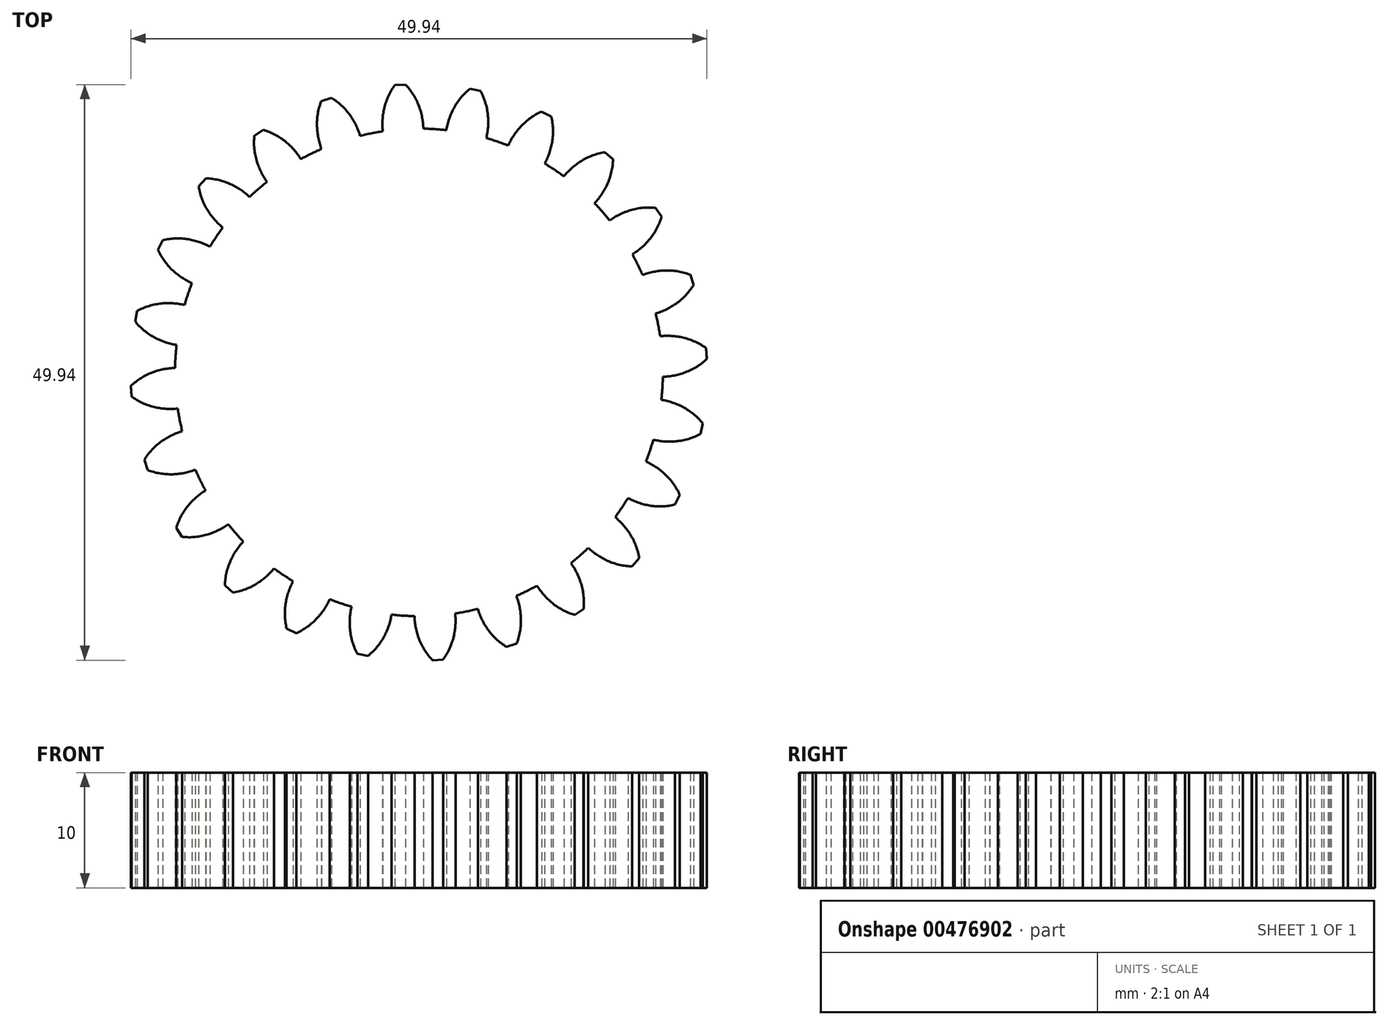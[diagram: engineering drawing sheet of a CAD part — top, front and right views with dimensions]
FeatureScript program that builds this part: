
annotation { "Feature Type Name" : "Feature", "Feature Type Description" : "" }
export const myFeature = defineFeature(function(context is Context, id is Id, definition is map)
    precondition{}
    {
        {
            var Q0;
            Q0=qCreatedBy(makeId("Top.planeOp"),FACE);
            var sketch = newSketch(context, id + "F0", { "sketchPlane" : qUnion([Q0])});
            skCircle(sketch, "E0", {"center": v(0, 0) * mm, "radius": 21.15 * mm});
            skCircle(sketch, "E1", {"center": v(0, 0) * mm, "radius": 23.1 * mm, "construction": true});
            skCircle(sketch, "E2", {"center": v(0, 0) * mm, "radius": 25 * mm, "construction": true});
            skLineSegment(sketch, "E3", {"start": v(0, 0) * mm, "end": v(0, 49.03) * mm, "construction": true});
            skLineSegment(sketch, "E4", {"start": v(0, 0) * mm, "end": v(-2.71, 41.35) * mm, "construction": true});
            skLineSegment(sketch, "E5", {"start": v(0, 23.1) * mm, "end": v(-29.6, 23.1) * mm, "construction": true});
            skLineSegment(sketch, "E6", {"start": v(-29.6, 23.1) * mm, "end": v(0, 23.1) * mm, "construction": true});
            skLineSegment(sketch, "E7", {"start": v(0, 23.1) * mm, "end": v(-33.56, 10.88) * mm, "construction": true});
            skCircle(sketch, "E8", {"center": v(0, 23.1) * mm, "radius": 5.75 * mm, "construction": true});
            skCircle(sketch, "E9", {"center": v(0, 0) * mm, "radius": 21.7 * mm, "construction": true});
            skArc(sketch, "E10", {"start": v(-1.67, 25.44) * mm, "mid": v(-9.32, 16.86) * mm, "end": v(-1.18, 24.97) * mm, "construction": true});
            skArc(sketch, "E11", {"start": v(0, 23.1) * mm, "mid": v(-0.5, 24.1) * mm, "end": v(-1.17, 24.97) * mm});
            skArc(sketch, "E12", {"start": v(0.38, 21.15) * mm, "mid": v(0.27, 22.14) * mm, "end": v(0, 23.1) * mm});
            skArc(sketch, "E13.MirrorCS", {"start": v(-3.14, 20.92) * mm, "mid": v(-3.16, 21.91) * mm, "end": v(-3.02, 22.9) * mm});
            skArc(sketch, "E14.MirrorCS", {"start": v(-3.02, 22.9) * mm, "mid": v(-2.66, 23.95) * mm, "end": v(-2.1, 24.91) * mm});
            skPoint(sketch, "E15.orphan", {"position": v(-1.67, 25.44) * mm});
            skLineSegment(sketch, "E16", {"start": v(-2.1, 24.91) * mm, "end": v(-1.17, 24.97) * mm});
            skArc(sketch, "E17.1.0", {"start": v(-8.84, 21.34) * mm, "mid": v(-8.77, 22.45) * mm, "end": v(-8.47, 23.52) * mm});
            skArc(sketch, "E17.1.1", {"start": v(-8.45, 19.4) * mm, "mid": v(-8.72, 20.35) * mm, "end": v(-8.84, 21.34) * mm});
            skArc(sketch, "E17.1.2", {"start": v(-5.98, 22.31) * mm, "mid": v(-6.71, 23.15) * mm, "end": v(-7.6, 23.82) * mm});
            skArc(sketch, "E17.1.3", {"start": v(-5.1, 20.53) * mm, "mid": v(-5.47, 21.46) * mm, "end": v(-5.98, 22.31) * mm});
            skLineSegment(sketch, "E17.1.4", {"start": v(-8.47, 23.52) * mm, "end": v(-7.6, 23.82) * mm});
            skArc(sketch, "E17.2.0", {"start": v(-14.06, 18.33) * mm, "mid": v(-14.28, 19.42) * mm, "end": v(-14.27, 20.52) * mm});
            skArc(sketch, "E17.2.1", {"start": v(-13.18, 16.54) * mm, "mid": v(-13.7, 17.4) * mm, "end": v(-14.06, 18.33) * mm});
            skArc(sketch, "E17.2.2", {"start": v(-11.55, 20) * mm, "mid": v(-12.47, 20.62) * mm, "end": v(-13.5, 21.04) * mm});
            skArc(sketch, "E17.2.3", {"start": v(-10.24, 18.5) * mm, "mid": v(-10.83, 19.3) * mm, "end": v(-11.55, 20) * mm});
            skLineSegment(sketch, "E17.2.4", {"start": v(-14.27, 20.52) * mm, "end": v(-13.5, 21.04) * mm});
            skArc(sketch, "E17.3.0", {"start": v(-18.33, 14.06) * mm, "mid": v(-18.82, 15.06) * mm, "end": v(-19.1, 16.13) * mm});
            skArc(sketch, "E17.3.1", {"start": v(-17, 12.57) * mm, "mid": v(-17.73, 13.26) * mm, "end": v(-18.33, 14.06) * mm});
            skArc(sketch, "E17.3.2", {"start": v(-16.33, 16.33) * mm, "mid": v(-17.39, 16.7) * mm, "end": v(-18.49, 16.83) * mm});
            skArc(sketch, "E17.3.3", {"start": v(-14.68, 15.22) * mm, "mid": v(-15.46, 15.85) * mm, "end": v(-16.33, 16.33) * mm});
            skLineSegment(sketch, "E17.3.4", {"start": v(-19.1, 16.13) * mm, "end": v(-18.49, 16.83) * mm});
            skArc(sketch, "E17.4.0", {"start": v(-21.34, 8.84) * mm, "mid": v(-22.07, 9.68) * mm, "end": v(-22.62, 10.64) * mm});
            skArc(sketch, "E17.4.1", {"start": v(-19.68, 7.74) * mm, "mid": v(-20.56, 8.22) * mm, "end": v(-21.34, 8.84) * mm});
            skArc(sketch, "E17.4.2", {"start": v(-20, 11.55) * mm, "mid": v(-21.11, 11.62) * mm, "end": v(-22.21, 11.47) * mm});
            skArc(sketch, "E17.4.3", {"start": v(-18.12, 10.9) * mm, "mid": v(-19.04, 11.3) * mm, "end": v(-20, 11.55) * mm});
            skLineSegment(sketch, "E17.4.4", {"start": v(-22.62, 10.64) * mm, "end": v(-22.21, 11.47) * mm});
            skArc(sketch, "E17.5.0", {"start": v(-22.9, 3.02) * mm, "mid": v(-23.82, 3.63) * mm, "end": v(-24.6, 4.42) * mm});
            skArc(sketch, "E17.5.1", {"start": v(-21.02, 2.38) * mm, "mid": v(-21.99, 2.62) * mm, "end": v(-22.9, 3.02) * mm});
            skArc(sketch, "E17.5.2", {"start": v(-22.31, 5.98) * mm, "mid": v(-23.4, 5.76) * mm, "end": v(-24.42, 5.33) * mm});
            skArc(sketch, "E17.5.3", {"start": v(-20.33, 5.84) * mm, "mid": v(-21.31, 6) * mm, "end": v(-22.31, 5.98) * mm});
            skLineSegment(sketch, "E17.5.4", {"start": v(-24.6, 4.42) * mm, "end": v(-24.42, 5.33) * mm});
            skArc(sketch, "E17.6.0", {"start": v(-22.9, -3.02) * mm, "mid": v(-23.95, -2.66) * mm, "end": v(-24.91, -2.1) * mm});
            skArc(sketch, "E17.6.1", {"start": v(-20.92, -3.14) * mm, "mid": v(-21.91, -3.16) * mm, "end": v(-22.9, -3.02) * mm});
            skArc(sketch, "E17.6.2", {"start": v(-23.1, 0) * mm, "mid": v(-24.1, -0.5) * mm, "end": v(-24.97, -1.17) * mm});
            skArc(sketch, "E17.6.3", {"start": v(-21.15, 0.38) * mm, "mid": v(-22.14, 0.27) * mm, "end": v(-23.1, 0) * mm});
            skLineSegment(sketch, "E17.6.4", {"start": v(-24.91, -2.1) * mm, "end": v(-24.97, -1.17) * mm});
            skArc(sketch, "E17.7.0", {"start": v(-21.34, -8.84) * mm, "mid": v(-22.45, -8.77) * mm, "end": v(-23.52, -8.47) * mm});
            skArc(sketch, "E17.7.1", {"start": v(-19.4, -8.45) * mm, "mid": v(-20.35, -8.72) * mm, "end": v(-21.34, -8.84) * mm});
            skArc(sketch, "E17.7.2", {"start": v(-22.31, -5.98) * mm, "mid": v(-23.15, -6.71) * mm, "end": v(-23.82, -7.6) * mm});
            skArc(sketch, "E17.7.3", {"start": v(-20.53, -5.1) * mm, "mid": v(-21.46, -5.47) * mm, "end": v(-22.31, -5.98) * mm});
            skLineSegment(sketch, "E17.7.4", {"start": v(-23.52, -8.47) * mm, "end": v(-23.82, -7.6) * mm});
            skArc(sketch, "E17.8.0", {"start": v(-18.33, -14.06) * mm, "mid": v(-19.42, -14.28) * mm, "end": v(-20.52, -14.27) * mm});
            skArc(sketch, "E17.8.1", {"start": v(-16.54, -13.18) * mm, "mid": v(-17.4, -13.7) * mm, "end": v(-18.33, -14.06) * mm});
            skArc(sketch, "E17.8.2", {"start": v(-20, -11.55) * mm, "mid": v(-20.62, -12.47) * mm, "end": v(-21.04, -13.5) * mm});
            skArc(sketch, "E17.8.3", {"start": v(-18.5, -10.24) * mm, "mid": v(-19.3, -10.83) * mm, "end": v(-20, -11.55) * mm});
            skLineSegment(sketch, "E17.8.4", {"start": v(-20.52, -14.27) * mm, "end": v(-21.04, -13.5) * mm});
            skArc(sketch, "E17.9.0", {"start": v(-14.06, -18.33) * mm, "mid": v(-15.06, -18.82) * mm, "end": v(-16.13, -19.1) * mm});
            skArc(sketch, "E17.9.1", {"start": v(-12.57, -17) * mm, "mid": v(-13.26, -17.73) * mm, "end": v(-14.06, -18.33) * mm});
            skArc(sketch, "E17.9.2", {"start": v(-16.33, -16.33) * mm, "mid": v(-16.7, -17.39) * mm, "end": v(-16.83, -18.49) * mm});
            skArc(sketch, "E17.9.3", {"start": v(-15.22, -14.68) * mm, "mid": v(-15.85, -15.46) * mm, "end": v(-16.33, -16.33) * mm});
            skLineSegment(sketch, "E17.9.4", {"start": v(-16.13, -19.1) * mm, "end": v(-16.83, -18.49) * mm});
            skArc(sketch, "E17.10.0", {"start": v(-8.84, -21.34) * mm, "mid": v(-9.68, -22.07) * mm, "end": v(-10.64, -22.62) * mm});
            skArc(sketch, "E17.10.1", {"start": v(-7.74, -19.68) * mm, "mid": v(-8.22, -20.56) * mm, "end": v(-8.84, -21.34) * mm});
            skArc(sketch, "E17.10.2", {"start": v(-11.55, -20) * mm, "mid": v(-11.62, -21.11) * mm, "end": v(-11.47, -22.21) * mm});
            skArc(sketch, "E17.10.3", {"start": v(-10.9, -18.12) * mm, "mid": v(-11.3, -19.04) * mm, "end": v(-11.55, -20) * mm});
            skLineSegment(sketch, "E17.10.4", {"start": v(-10.64, -22.62) * mm, "end": v(-11.47, -22.21) * mm});
            skArc(sketch, "E17.11.0", {"start": v(-3.02, -22.9) * mm, "mid": v(-3.63, -23.82) * mm, "end": v(-4.42, -24.6) * mm});
            skArc(sketch, "E17.11.1", {"start": v(-2.38, -21.02) * mm, "mid": v(-2.62, -21.99) * mm, "end": v(-3.02, -22.9) * mm});
            skArc(sketch, "E17.11.2", {"start": v(-5.98, -22.31) * mm, "mid": v(-5.76, -23.4) * mm, "end": v(-5.33, -24.42) * mm});
            skArc(sketch, "E17.11.3", {"start": v(-5.84, -20.33) * mm, "mid": v(-6, -21.31) * mm, "end": v(-5.98, -22.31) * mm});
            skLineSegment(sketch, "E17.11.4", {"start": v(-4.42, -24.6) * mm, "end": v(-5.33, -24.42) * mm});
            skArc(sketch, "E17.12.0", {"start": v(3.02, -22.9) * mm, "mid": v(2.66, -23.95) * mm, "end": v(2.1, -24.91) * mm});
            skArc(sketch, "E17.12.1", {"start": v(3.14, -20.92) * mm, "mid": v(3.16, -21.91) * mm, "end": v(3.02, -22.9) * mm});
            skArc(sketch, "E17.12.2", {"start": v(0, -23.1) * mm, "mid": v(0.5, -24.1) * mm, "end": v(1.17, -24.97) * mm});
            skArc(sketch, "E17.12.3", {"start": v(-0.38, -21.15) * mm, "mid": v(-0.27, -22.14) * mm, "end": v(0, -23.1) * mm});
            skLineSegment(sketch, "E17.12.4", {"start": v(2.1, -24.91) * mm, "end": v(1.17, -24.97) * mm});
            skArc(sketch, "E17.13.0", {"start": v(8.84, -21.34) * mm, "mid": v(8.77, -22.45) * mm, "end": v(8.47, -23.52) * mm});
            skArc(sketch, "E17.13.1", {"start": v(8.45, -19.4) * mm, "mid": v(8.72, -20.35) * mm, "end": v(8.84, -21.34) * mm});
            skArc(sketch, "E17.13.2", {"start": v(5.98, -22.31) * mm, "mid": v(6.71, -23.15) * mm, "end": v(7.6, -23.82) * mm});
            skArc(sketch, "E17.13.3", {"start": v(5.1, -20.53) * mm, "mid": v(5.47, -21.46) * mm, "end": v(5.98, -22.31) * mm});
            skLineSegment(sketch, "E17.13.4", {"start": v(8.47, -23.52) * mm, "end": v(7.6, -23.82) * mm});
            skArc(sketch, "E17.14.0", {"start": v(14.06, -18.33) * mm, "mid": v(14.28, -19.42) * mm, "end": v(14.27, -20.52) * mm});
            skArc(sketch, "E17.14.1", {"start": v(13.18, -16.54) * mm, "mid": v(13.7, -17.4) * mm, "end": v(14.06, -18.33) * mm});
            skArc(sketch, "E17.14.2", {"start": v(11.55, -20) * mm, "mid": v(12.47, -20.62) * mm, "end": v(13.5, -21.04) * mm});
            skArc(sketch, "E17.14.3", {"start": v(10.24, -18.5) * mm, "mid": v(10.83, -19.3) * mm, "end": v(11.55, -20) * mm});
            skLineSegment(sketch, "E17.14.4", {"start": v(14.27, -20.52) * mm, "end": v(13.5, -21.04) * mm});
            skArc(sketch, "E17.15.0", {"start": v(18.33, -14.06) * mm, "mid": v(18.82, -15.06) * mm, "end": v(19.1, -16.13) * mm});
            skArc(sketch, "E17.15.1", {"start": v(17, -12.57) * mm, "mid": v(17.73, -13.26) * mm, "end": v(18.33, -14.06) * mm});
            skArc(sketch, "E17.15.2", {"start": v(16.33, -16.33) * mm, "mid": v(17.39, -16.7) * mm, "end": v(18.49, -16.83) * mm});
            skArc(sketch, "E17.15.3", {"start": v(14.68, -15.22) * mm, "mid": v(15.46, -15.85) * mm, "end": v(16.33, -16.33) * mm});
            skLineSegment(sketch, "E17.15.4", {"start": v(19.1, -16.13) * mm, "end": v(18.49, -16.83) * mm});
            skArc(sketch, "E17.16.0", {"start": v(21.34, -8.84) * mm, "mid": v(22.07, -9.68) * mm, "end": v(22.62, -10.64) * mm});
            skArc(sketch, "E17.16.1", {"start": v(19.68, -7.74) * mm, "mid": v(20.56, -8.22) * mm, "end": v(21.34, -8.84) * mm});
            skArc(sketch, "E17.16.2", {"start": v(20, -11.55) * mm, "mid": v(21.11, -11.62) * mm, "end": v(22.21, -11.47) * mm});
            skArc(sketch, "E17.16.3", {"start": v(18.12, -10.9) * mm, "mid": v(19.04, -11.3) * mm, "end": v(20, -11.55) * mm});
            skLineSegment(sketch, "E17.16.4", {"start": v(22.62, -10.64) * mm, "end": v(22.21, -11.47) * mm});
            skArc(sketch, "E17.17.0", {"start": v(22.9, -3.02) * mm, "mid": v(23.82, -3.63) * mm, "end": v(24.6, -4.42) * mm});
            skArc(sketch, "E17.17.1", {"start": v(21.02, -2.38) * mm, "mid": v(21.99, -2.62) * mm, "end": v(22.9, -3.02) * mm});
            skArc(sketch, "E17.17.2", {"start": v(22.31, -5.98) * mm, "mid": v(23.4, -5.76) * mm, "end": v(24.42, -5.33) * mm});
            skArc(sketch, "E17.17.3", {"start": v(20.33, -5.84) * mm, "mid": v(21.31, -6) * mm, "end": v(22.31, -5.98) * mm});
            skLineSegment(sketch, "E17.17.4", {"start": v(24.6, -4.42) * mm, "end": v(24.42, -5.33) * mm});
            skArc(sketch, "E17.18.0", {"start": v(22.9, 3.02) * mm, "mid": v(23.95, 2.66) * mm, "end": v(24.91, 2.1) * mm});
            skArc(sketch, "E17.18.1", {"start": v(20.92, 3.14) * mm, "mid": v(21.91, 3.16) * mm, "end": v(22.9, 3.02) * mm});
            skArc(sketch, "E17.18.2", {"start": v(23.1, 0) * mm, "mid": v(24.1, 0.5) * mm, "end": v(24.97, 1.17) * mm});
            skArc(sketch, "E17.18.3", {"start": v(21.15, -0.38) * mm, "mid": v(22.14, -0.27) * mm, "end": v(23.1, 0) * mm});
            skLineSegment(sketch, "E17.18.4", {"start": v(24.91, 2.1) * mm, "end": v(24.97, 1.17) * mm});
            skArc(sketch, "E17.19.0", {"start": v(21.34, 8.84) * mm, "mid": v(22.45, 8.77) * mm, "end": v(23.52, 8.47) * mm});
            skArc(sketch, "E17.19.1", {"start": v(19.4, 8.45) * mm, "mid": v(20.35, 8.72) * mm, "end": v(21.34, 8.84) * mm});
            skArc(sketch, "E17.19.2", {"start": v(22.31, 5.98) * mm, "mid": v(23.15, 6.71) * mm, "end": v(23.82, 7.6) * mm});
            skArc(sketch, "E17.19.3", {"start": v(20.53, 5.1) * mm, "mid": v(21.46, 5.47) * mm, "end": v(22.31, 5.98) * mm});
            skLineSegment(sketch, "E17.19.4", {"start": v(23.52, 8.47) * mm, "end": v(23.82, 7.6) * mm});
            skArc(sketch, "E17.20.0", {"start": v(18.33, 14.06) * mm, "mid": v(19.42, 14.28) * mm, "end": v(20.52, 14.27) * mm});
            skArc(sketch, "E17.20.1", {"start": v(16.54, 13.18) * mm, "mid": v(17.4, 13.7) * mm, "end": v(18.33, 14.06) * mm});
            skArc(sketch, "E17.20.2", {"start": v(20, 11.55) * mm, "mid": v(20.62, 12.47) * mm, "end": v(21.04, 13.5) * mm});
            skArc(sketch, "E17.20.3", {"start": v(18.5, 10.24) * mm, "mid": v(19.3, 10.83) * mm, "end": v(20, 11.55) * mm});
            skLineSegment(sketch, "E17.20.4", {"start": v(20.52, 14.27) * mm, "end": v(21.04, 13.5) * mm});
            skArc(sketch, "E17.21.0", {"start": v(14.06, 18.33) * mm, "mid": v(15.06, 18.82) * mm, "end": v(16.13, 19.1) * mm});
            skArc(sketch, "E17.21.1", {"start": v(12.57, 17) * mm, "mid": v(13.26, 17.73) * mm, "end": v(14.06, 18.33) * mm});
            skArc(sketch, "E17.21.2", {"start": v(16.33, 16.33) * mm, "mid": v(16.7, 17.39) * mm, "end": v(16.83, 18.49) * mm});
            skArc(sketch, "E17.21.3", {"start": v(15.22, 14.68) * mm, "mid": v(15.85, 15.46) * mm, "end": v(16.33, 16.33) * mm});
            skLineSegment(sketch, "E17.21.4", {"start": v(16.13, 19.1) * mm, "end": v(16.83, 18.49) * mm});
            skArc(sketch, "E17.22.0", {"start": v(8.84, 21.34) * mm, "mid": v(9.68, 22.07) * mm, "end": v(10.64, 22.62) * mm});
            skArc(sketch, "E17.22.1", {"start": v(7.74, 19.68) * mm, "mid": v(8.22, 20.56) * mm, "end": v(8.84, 21.34) * mm});
            skArc(sketch, "E17.22.2", {"start": v(11.55, 20) * mm, "mid": v(11.62, 21.11) * mm, "end": v(11.47, 22.21) * mm});
            skArc(sketch, "E17.22.3", {"start": v(10.9, 18.12) * mm, "mid": v(11.3, 19.04) * mm, "end": v(11.55, 20) * mm});
            skLineSegment(sketch, "E17.22.4", {"start": v(10.64, 22.62) * mm, "end": v(11.47, 22.21) * mm});
            skArc(sketch, "E17.23.0", {"start": v(3.02, 22.9) * mm, "mid": v(3.63, 23.82) * mm, "end": v(4.42, 24.6) * mm});
            skArc(sketch, "E17.23.1", {"start": v(2.38, 21.02) * mm, "mid": v(2.62, 21.99) * mm, "end": v(3.02, 22.9) * mm});
            skArc(sketch, "E17.23.2", {"start": v(5.98, 22.31) * mm, "mid": v(5.76, 23.4) * mm, "end": v(5.33, 24.42) * mm});
            skArc(sketch, "E17.23.3", {"start": v(5.84, 20.33) * mm, "mid": v(6, 21.31) * mm, "end": v(5.98, 22.31) * mm});
            skLineSegment(sketch, "E17.23.4", {"start": v(4.42, 24.6) * mm, "end": v(5.33, 24.42) * mm});
            skSolve(sketch);
        }
        {
            var Q0;
            Q0 = qSketchRegion(id + "F0", true);
            extrude(context, id + "F1", {"entities" : qUnion([Q0]), "depth" : 10 * mm});
        }
    });
